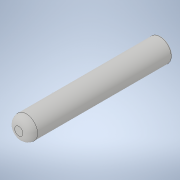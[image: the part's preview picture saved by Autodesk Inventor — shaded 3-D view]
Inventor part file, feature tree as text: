
AUTODESK INVENTOR PART (.ipt)
format: ipt  version: 2020 (Build 240168000, 168)  size: 105,984 bytes
history: native  units: mm
features: fillet x2, extrude x1, sketch x1
ambient origin geometry x8: Origin, YZ Plane, XZ Plane, XY Plane, X Axis, Y Axis, Z Axis, Center Point
bodies: Solid1 (feature_tree)
feature tree (4):
  extrude  "Extrusion1"  Depth=484.0mm TaperAngle=0.0deg
  fillet  "Fillet1"  Radius=25.0mm
  fillet  "Fillet4"  Radius=5.0mm
  sketch  "Sketch1"  dims[d0=78.0mm d1=484.0mm d2=0.0mm d3=25.0mm d6=5.0mm]
